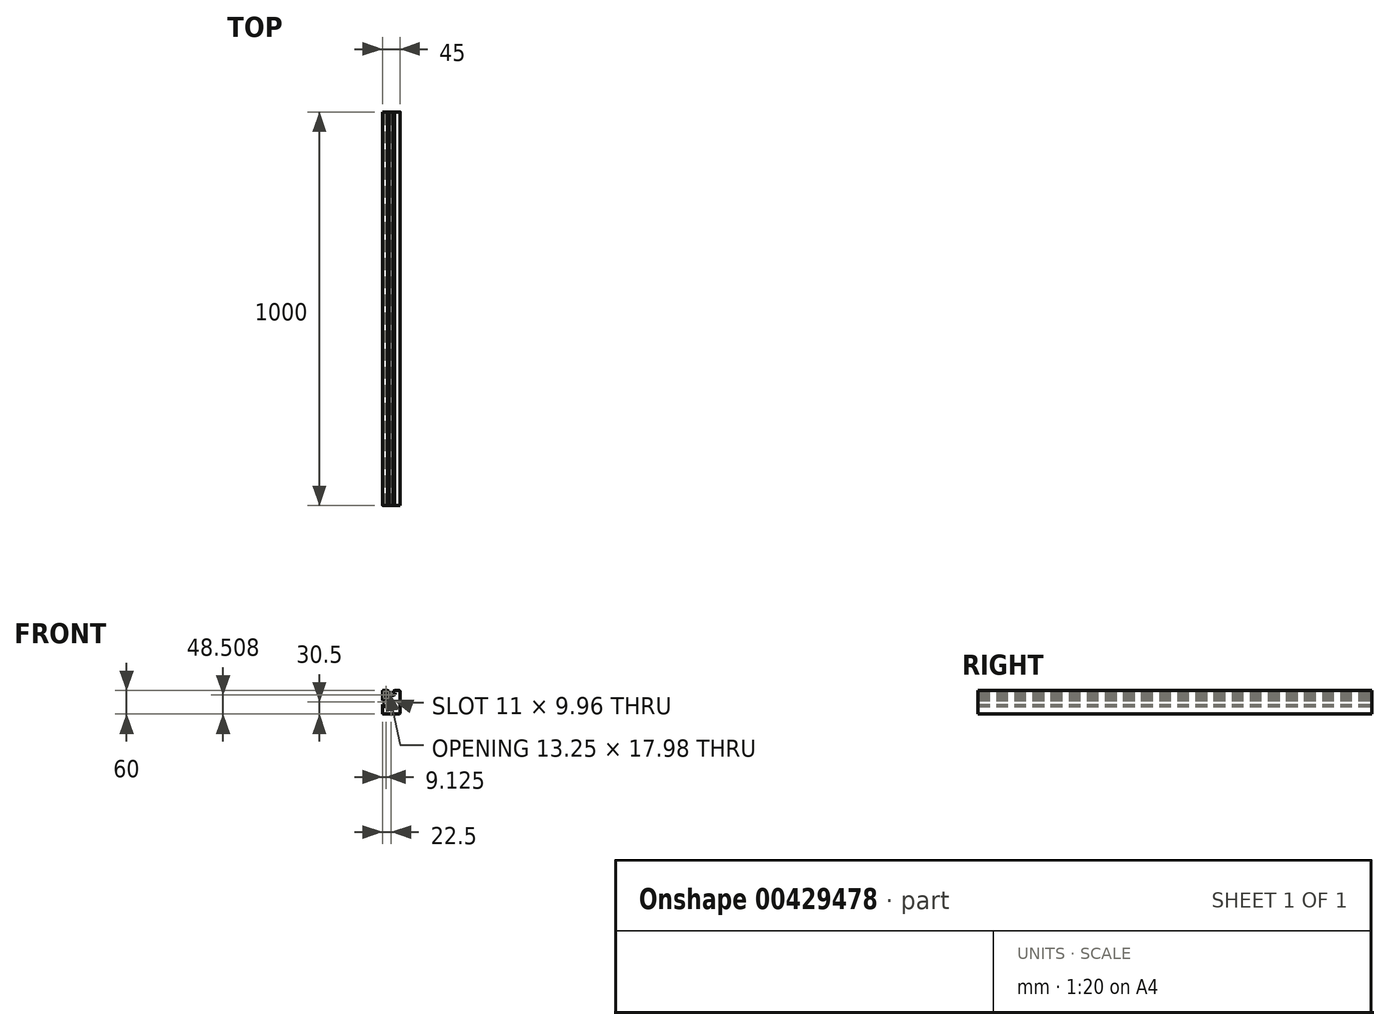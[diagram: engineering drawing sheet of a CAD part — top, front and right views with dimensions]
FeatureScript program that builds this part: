
annotation { "Feature Type Name" : "Feature", "Feature Type Description" : "" }
export const myFeature = defineFeature(function(context is Context, id is Id, definition is map)
    precondition{}
    {
        {
            var Q0;
            Q0=qCreatedBy(makeId("Front.planeOp"),FACE);
            var sketch = newSketch(context, id + "F0", { "sketchPlane" : qUnion([Q0])});
            skLineSegment(sketch, "E0.bottom", {"start": v(-22.5, 30) * mm, "end": v(22.5, 30) * mm});
            skLineSegment(sketch, "E0.top", {"start": v(-22.5, -30) * mm, "end": v(22.5, -30) * mm});
            skLineSegment(sketch, "E0.left", {"start": v(-22.5, 30) * mm, "end": v(-22.5, -30) * mm});
            skLineSegment(sketch, "E0.right", {"start": v(22.5, 30) * mm, "end": v(22.5, -30) * mm});
            skSolve(sketch);
        }
        {
            var Q0;
            Q0=qSketchRegion(id+"F0",true);
            extrude(context, id + "F1", {"entities" : qUnion([Q0]), "depth" : 1000 * mm});
        }
        {
            var Q0;
            Q0=makeQuery(id+"F1.opExtrude","SWEPT_EDGE",EDGE,{"disambiguationData":[OSD([sQuery(id+"F0.wireOp",EDGE,"E0.top"),sQuery(id+"F0.wireOp",EDGE,"E0.left")])]});
            var Q1;
            Q1=makeQuery(id+"F1.opExtrude","SWEPT_EDGE",EDGE,{"disambiguationData":[OSD([sQuery(id+"F0.wireOp",EDGE,"E0.bottom"),sQuery(id+"F0.wireOp",EDGE,"E0.left")])]});
            var Q2;
            Q2=makeQuery(id+"F1.opExtrude","SWEPT_EDGE",EDGE,{"disambiguationData":[OSD([sQuery(id+"F0.wireOp",EDGE,"E0.top"),sQuery(id+"F0.wireOp",EDGE,"E0.right")])]});
            var Q3;
            Q3=makeQuery(id+"F1.opExtrude","SWEPT_EDGE",EDGE,{"disambiguationData":[OSD([sQuery(id+"F0.wireOp",EDGE,"E0.bottom"),sQuery(id+"F0.wireOp",EDGE,"E0.right")])]});
            fillet(context, id + "F2", {"entities" : qUnion([Q0, Q1, Q2, Q3]), "radius" : 3 * mm, "tangentPropagation" : true, "allowEdgeOverflow" : false});
        }
        {
            var Q0;
            Q0=qCreatedBy(makeId("Front.planeOp"),FACE);
            var sketch = newSketch(context, id + "F3", { "sketchPlane" : qUnion([Q0])});
            skCircle(sketch, "E1", {"center": v(0, 0) * mm, "radius": 5 * mm});
            skSolve(sketch);
        }
        {
            var Q0;
            Q0=qSketchRegion(id+"F3",true);
            extrude(context, id + "F4", {"entities" : qUnion([Q0]), "operationType" : NewBodyOperationType.REMOVE, "endBound" : BoundingType.THROUGH_ALL, "depth" : 25 * mm});
        }
        {
            var Q0;
            Q0=qCreatedBy(makeId("Front.planeOp"),FACE);
            var sketch = newSketch(context, id + "F5", { "sketchPlane" : qUnion([Q0])});
            skLineSegment(sketch, "E2.bottom", {"start": v(-9, 30) * mm, "end": v(9, 30) * mm});
            skLineSegment(sketch, "E2.top", {"start": v(-9, 29) * mm, "end": v(-5, 29) * mm});
            skLineSegment(sketch, "E2.left", {"start": v(-9, 30) * mm, "end": v(-9, 29) * mm});
            skLineSegment(sketch, "E2.right", {"start": v(9, 30) * mm, "end": v(9, 29) * mm});
            skLineSegment(sketch, "E3.left", {"start": v(-5, 29) * mm, "end": v(-5, 24) * mm});
            skLineSegment(sketch, "E3.right", {"start": v(5, 29) * mm, "end": v(5, 24) * mm});
            skPoint(sketch, "E4.firstSnap0", {"position": v(0, 24) * mm});
            skLineSegment(sketch, "E4.bottom", {"start": v(-10.25, 24) * mm, "end": v(-5, 24) * mm});
            skLineSegment(sketch, "E4.top", {"start": v(-5.05, 17) * mm, "end": v(5.05, 17) * mm});
            skLineSegment(sketch, "E4.left", {"start": v(-10.25, 24) * mm, "end": v(-10.25, 20) * mm});
            skLineSegment(sketch, "E4.right", {"start": v(10.25, 24) * mm, "end": v(10.25, 20) * mm});
            skLineSegment(sketch, "E5.trimOffspring", {"start": v(5, 24) * mm, "end": v(10.25, 24) * mm});
            skLineSegment(sketch, "E6.trimOffspring", {"start": v(5, 29) * mm, "end": v(9, 29) * mm});
            skLineSegment(sketch, "E7", {"start": v(-10.25, 20) * mm, "end": v(-5.05, 17) * mm});
            skLineSegment(sketch, "E8", {"start": v(5.05, 17) * mm, "end": v(10.25, 20) * mm});
            skSolve(sketch);
        }
        {
            var Q0;
            Q0=qSketchRegion(id+"F5",true);
            extrude(context, id + "F6", {"entities" : qUnion([Q0]), "operationType" : NewBodyOperationType.REMOVE, "endBound" : BoundingType.THROUGH_ALL, "depth" : 25 * mm});
        }
        {
            var Q0;
            Q0=qCreatedBy(makeId("Front.planeOp"),FACE);
            var sketch = newSketch(context, id + "F7", { "sketchPlane" : qUnion([Q0])});
            skLineSegment(sketch, "E9.bottom", {"start": v(-22.5, 9) * mm, "end": v(-21.5, 9) * mm});
            skLineSegment(sketch, "E9.top", {"start": v(-22.5, -9) * mm, "end": v(-21.5, -9) * mm});
            skLineSegment(sketch, "E9.left", {"start": v(-22.5, 9) * mm, "end": v(-22.5, -9) * mm});
            skLineSegment(sketch, "E9.right", {"start": v(-21.5, 9) * mm, "end": v(-21.5, 5) * mm});
            skLineSegment(sketch, "E10.bottom", {"start": v(-21.5, 5) * mm, "end": v(-16.5, 5) * mm});
            skLineSegment(sketch, "E10.top", {"start": v(-21.5, -5) * mm, "end": v(-16.5, -5) * mm});
            skLineSegment(sketch, "E11.bottom", {"start": v(-16.5, 10.25) * mm, "end": v(-12.5, 10.25) * mm});
            skLineSegment(sketch, "E11.top", {"start": v(-16.5, -10.25) * mm, "end": v(-12.5, -10.25) * mm});
            skLineSegment(sketch, "E11.left", {"start": v(-16.5, 10.25) * mm, "end": v(-16.5, 5) * mm});
            skLineSegment(sketch, "E11.right", {"start": v(-9.5, 5.05) * mm, "end": v(-9.5, -5.05) * mm});
            skLineSegment(sketch, "E12.trimOffspring", {"start": v(-16.5, -5) * mm, "end": v(-16.5, -10.25) * mm});
            skLineSegment(sketch, "E13.trimOffspring", {"start": v(-21.5, -5) * mm, "end": v(-21.5, -9) * mm});
            skLineSegment(sketch, "E14", {"start": v(-12.5, 10.25) * mm, "end": v(-9.5, 5.05) * mm});
            skLineSegment(sketch, "E15", {"start": v(-9.5, -5.05) * mm, "end": v(-12.5, -10.25) * mm});
            skSolve(sketch);
        }
        {
            var Q0;
            Q0=qSketchRegion(id+"F7",true);
            extrude(context, id + "F8", {"entities" : qUnion([Q0]), "operationType" : NewBodyOperationType.REMOVE, "endBound" : BoundingType.THROUGH_ALL, "depth" : 25 * mm});
        }
        {
            var Q0;
            Q0=qCreatedBy(makeId("Front.planeOp"),FACE);
            var sketch = newSketch(context, id + "F9", { "sketchPlane" : qUnion([Q0])});
            skArc(sketch, "E16", {"start": v(1.04, 5.9) * mm, "mid": v(0, 6) * mm, "end": v(-1.04, 5.9) * mm});
            skLineSegment(sketch, "E17", {"start": v(-1.04, 5.9) * mm, "end": v(0, 0) * mm});
            skLineSegment(sketch, "E18", {"start": v(0, 0) * mm, "end": v(1.04, 5.9) * mm});
            skSolve(sketch);
        }
        {
            var Q0;
            Q0=qSketchRegion(id+"F9",true);
            extrude(context, id + "F10", {"entities" : qUnion([Q0]), "operationType" : NewBodyOperationType.REMOVE, "endBound" : BoundingType.THROUGH_ALL, "depth" : 25 * mm});
        }
        {
            var Q0;
            Q0=makeQuery(id+"F1.opExtrude","CAP_FACE",FACE,{"disambiguationData":[OSD([sQuery(id+"F0.wireOp",EDGE,"E0.bottom"),sQuery(id+"F0.wireOp",EDGE,"E0.top"),sQuery(id+"F0.wireOp",EDGE,"E0.left"),sQuery(id+"F0.wireOp",EDGE,"E0.right")])],"isStart":false});
            var sketch = newSketch(context, id + "F11", { "sketchPlane" : qUnion([Q0])});
            skSolve(sketch);
        }
        {
            var Q0;
            Q0=qCreatedBy(makeId("Front.planeOp"),FACE);
            var sketch = newSketch(context, id + "F12", { "sketchPlane" : qUnion([Q0])});
            skLineSegment(sketch, "E19.bottom", {"start": v(-20, 27.5) * mm, "end": v(-12.75, 27.5) * mm});
            skLineSegment(sketch, "E19.top", {"start": v(-20, 12.75) * mm, "end": v(-12.75, 12.75) * mm});
            skLineSegment(sketch, "E19.left", {"start": v(-20, 27.5) * mm, "end": v(-20, 12.75) * mm});
            skLineSegment(sketch, "E19.right", {"start": v(-12.75, 27.5) * mm, "end": v(-12.75, 12.75) * mm});
            skSolve(sketch);
        }
        {
            var Q0;
            Q0=makeQuery(id+"F12.imprint","IMPRINT",FACE,{"disambiguationData":[TD([[makeQuery(id+"F12.imprint","IMPRINT",EDGE,{"derivedFrom":sQuery(id+"F12.wireOp",EDGE,"E19.bottom")}),-1.0]])]});
            extrude(context, id + "F13", {"entities" : qUnion([Q0]), "operationType" : NewBodyOperationType.REMOVE, "endBound" : BoundingType.THROUGH_ALL, "depth" : 25 * mm});
        }
        {
            var Q0;
            Q0=makeQuery(id+"F13.boolean.opBoolean","COPY",EDGE,{"derivedFrom":makeQuery(id+"F13.opExtrude","SWEPT_EDGE",EDGE,{"disambiguationData":[OSD([sQuery(id+"F12.wireOp",EDGE,"E19.bottom"),sQuery(id+"F12.wireOp",EDGE,"E19.left")])]})});
            var Q1;
            Q1=makeQuery(id+"FcmsCtEJTRXYj0O_1.1.F13.boolean.opBoolean","COPY",EDGE,{"derivedFrom":makeQuery(id+"FcmsCtEJTRXYj0O_1.1.F13.opExtrude","SWEPT_EDGE",EDGE,{"disambiguationData":[OSD([sQuery(id+"F12.wireOp",EDGE,"E19.bottom"),sQuery(id+"F12.wireOp",EDGE,"E19.left")])]})});
            var Q2;
            Q2=makeQuery(id+"FTRXRFmJaNHCruk_1.1.F13.boolean.opBoolean","COPY",EDGE,{"derivedFrom":makeQuery(id+"FTRXRFmJaNHCruk_1.1.F13.opExtrude","SWEPT_EDGE",EDGE,{"disambiguationData":[OSD([sQuery(id+"F12.wireOp",EDGE,"E19.bottom"),sQuery(id+"F12.wireOp",EDGE,"E19.left")])]})});
            var Q3;
            Q3=makeQuery(id+"FTRXRFmJaNHCruk_1.1.FcmsCtEJTRXYj0O_1.1.F13.boolean.opBoolean","COPY",EDGE,{"derivedFrom":makeQuery(id+"FTRXRFmJaNHCruk_1.1.FcmsCtEJTRXYj0O_1.1.F13.opExtrude","SWEPT_EDGE",EDGE,{"disambiguationData":[OSD([sQuery(id+"F12.wireOp",EDGE,"E19.bottom"),sQuery(id+"F12.wireOp",EDGE,"E19.left")])]})});
            fillet(context, id + "F14", {"entities" : qUnion([Q0, Q1, Q2, Q3]), "radius" : 3 * mm, "tangentPropagation" : true, "allowEdgeOverflow" : false});
        }
        {
            var Q0;
            Q0=qCreatedBy(makeId("Front.planeOp"),FACE);
            var sketch = newSketch(context, id + "F15", { "sketchPlane" : qUnion([Q0])});
            skLineSegment(sketch, "E20", {"start": v(-12.75, 17.98) * mm, "end": v(-6.75, 14.52) * mm});
            skLineSegment(sketch, "E21", {"start": v(-6.75, 14.52) * mm, "end": v(-6.75, 9.52) * mm});
            skLineSegment(sketch, "E22", {"start": v(-6.75, 9.52) * mm, "end": v(-10.88, 9.52) * mm});
            skLineSegment(sketch, "E23", {"start": v(-10.88, 9.52) * mm, "end": v(-12.75, 12.75) * mm});
            skLineSegment(sketch, "E24", {"start": v(-12.75, 12.75) * mm, "end": v(-12.75, 17.98) * mm});
            skSolve(sketch);
        }
        {
            var Q0;
            Q0 = qSketchRegion(id + "F15", true);
            extrude(context, id + "F16", {"entities" : qUnion([Q0]), "operationType" : NewBodyOperationType.REMOVE, "endBound" : BoundingType.THROUGH_ALL, "depth" : 25 * mm});
        }
        {
            var Q0;
            Q0=makeQuery(id+"F8MlFY9KwXS7PmJ_1.1.F16.boolean.opBoolean","MERGE",EDGE,{"derivedFrom":[makeQuery(id+"FcmsCtEJTRXYj0O_1.1.F13.boolean.opBoolean","COPY",EDGE,{"derivedFrom":makeQuery(id+"FcmsCtEJTRXYj0O_1.1.F13.opExtrude","SWEPT_EDGE",EDGE,{"disambiguationData":[OSD([sQuery(id+"F12.wireOp",EDGE,"E19.top"),sQuery(id+"F12.wireOp",EDGE,"E19.right")])]})}),makeQuery(id+"F8MlFY9KwXS7PmJ_1.1.F16.opExtrude","SWEPT_EDGE",EDGE,{"disambiguationData":[OSD([sQuery(id+"F15.wireOp",EDGE,"E23"),sQuery(id+"F15.wireOp",EDGE,"E24")])]})]});
            var Q1;
            Q1=makeQuery(id+"F16.boolean.opBoolean","MERGE",EDGE,{"derivedFrom":[makeQuery(id+"F13.boolean.opBoolean","COPY",EDGE,{"derivedFrom":makeQuery(id+"F13.opExtrude","SWEPT_EDGE",EDGE,{"disambiguationData":[OSD([sQuery(id+"F12.wireOp",EDGE,"E19.top"),sQuery(id+"F12.wireOp",EDGE,"E19.right")])]})}),makeQuery(id+"F16.opExtrude","SWEPT_EDGE",EDGE,{"disambiguationData":[OSD([sQuery(id+"F15.wireOp",EDGE,"E23"),sQuery(id+"F15.wireOp",EDGE,"E24")])]})]});
            var Q2;
            Q2=makeQuery(id+"FwNXFRG0LKpJ2J5_1.1.F16.boolean.opBoolean","COPY",EDGE,{"derivedFrom":makeQuery(id+"FwNXFRG0LKpJ2J5_1.1.F16.opExtrude","SWEPT_EDGE",EDGE,{"disambiguationData":[OSD([sQuery(id+"F15.wireOp",EDGE,"E20"),sQuery(id+"F15.wireOp",EDGE,"E24")])]})});
            var Q3;
            Q3=makeQuery(id+"FwNXFRG0LKpJ2J5_1.1.F8MlFY9KwXS7PmJ_1.1.F16.boolean.opBoolean","COPY",EDGE,{"derivedFrom":makeQuery(id+"FwNXFRG0LKpJ2J5_1.1.F8MlFY9KwXS7PmJ_1.1.F16.opExtrude","SWEPT_EDGE",EDGE,{"disambiguationData":[OSD([sQuery(id+"F15.wireOp",EDGE,"E20"),sQuery(id+"F15.wireOp",EDGE,"E24")])]})});
            fillet(context, id + "F17", {"entities" : qUnion([Q0, Q1, Q2, Q3]), "radius" : 1 * mm, "tangentPropagation" : true, "allowEdgeOverflow" : false});
        }
        {
            var Q0;
            Q0=makeQuery(id+"F16.boolean.opBoolean","COPY",EDGE,{"derivedFrom":makeQuery(id+"F16.opExtrude","SWEPT_EDGE",EDGE,{"disambiguationData":[OSD([sQuery(id+"F15.wireOp",EDGE,"E22"),sQuery(id+"F15.wireOp",EDGE,"E23")])]})});
            var Q1;
            Q1=makeQuery(id+"F8MlFY9KwXS7PmJ_1.1.F16.boolean.opBoolean","COPY",EDGE,{"derivedFrom":makeQuery(id+"F8MlFY9KwXS7PmJ_1.1.F16.opExtrude","SWEPT_EDGE",EDGE,{"disambiguationData":[OSD([sQuery(id+"F15.wireOp",EDGE,"E22"),sQuery(id+"F15.wireOp",EDGE,"E23")])]})});
            var Q2;
            Q2=makeQuery(id+"FwNXFRG0LKpJ2J5_1.1.F8MlFY9KwXS7PmJ_1.1.F16.boolean.opBoolean","COPY",EDGE,{"derivedFrom":makeQuery(id+"FwNXFRG0LKpJ2J5_1.1.F8MlFY9KwXS7PmJ_1.1.F16.opExtrude","SWEPT_EDGE",EDGE,{"disambiguationData":[OSD([sQuery(id+"F15.wireOp",EDGE,"E22"),sQuery(id+"F15.wireOp",EDGE,"E23")])]})});
            var Q3;
            Q3=makeQuery(id+"FwNXFRG0LKpJ2J5_1.1.F16.boolean.opBoolean","COPY",EDGE,{"derivedFrom":makeQuery(id+"FwNXFRG0LKpJ2J5_1.1.F16.opExtrude","SWEPT_EDGE",EDGE,{"disambiguationData":[OSD([sQuery(id+"F15.wireOp",EDGE,"E21"),sQuery(id+"F15.wireOp",EDGE,"E22")])]})});
            fillet(context, id + "F18", {"entities" : qUnion([Q0, Q1, Q2, Q3]), "radius" : 2 * mm, "tangentPropagation" : true, "allowEdgeOverflow" : false});
        }
    });
